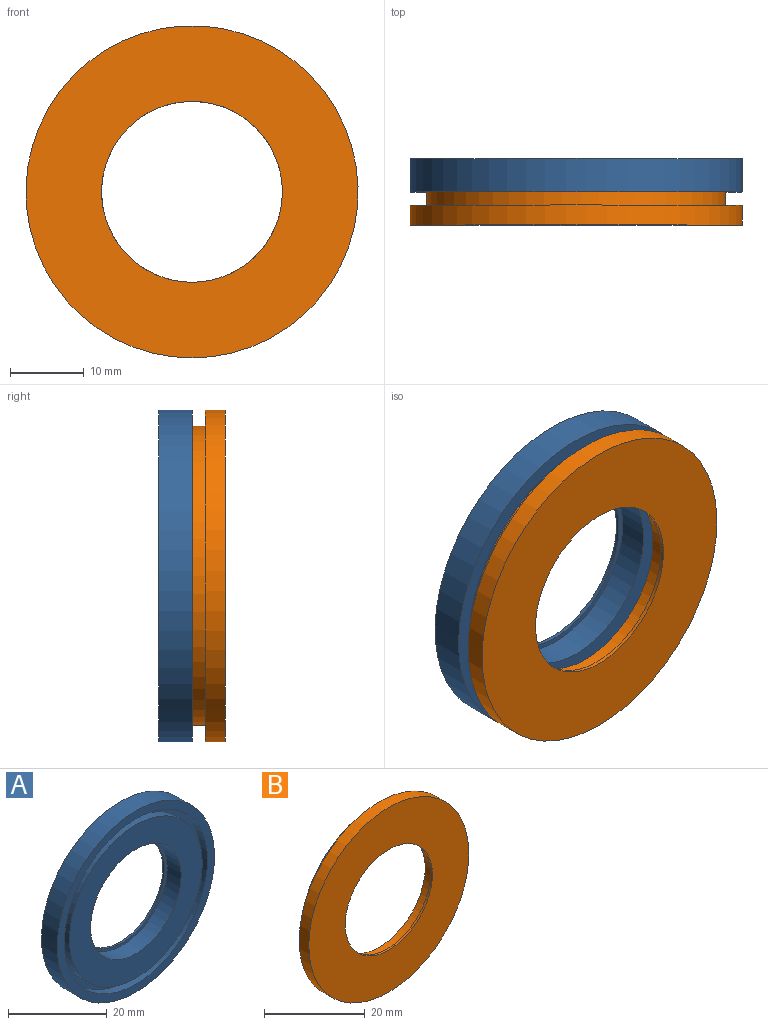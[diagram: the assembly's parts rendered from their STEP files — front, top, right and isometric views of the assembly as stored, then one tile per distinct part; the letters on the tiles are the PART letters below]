
ASSEMBLY  parts=2 mates=1
PART A: 10 faces, bbox 45x4.5x45 mm
  f0: plane 38x38mm, normal (0,-1,0), area 607.3mm2, adj f1,f7
  f1: cylinder r=12.95mm len=25.9mm, axis (0,1,0), area 325.5mm2, adj f0,f6
  f2: cylinder r=22.5mm len=45mm, axis (0,1,0), area 636.2mm2, adj f3,f4
  f3: plane 45x45mm, normal (0,-1,0), area 270.2mm2, adj f2,f8
  f4: plane 45x45mm, normal (0,1,0), area 1119mm2, adj f2,f5
  f5: cylinder r=12.25mm len=24.5mm, axis (0,1,0), area 38.5mm2, adj f4,f6
  f6: plane 25.9x25.9mm, normal (0,-1,0), area 55.4mm2, adj f1,f5
  f7: cylinder r=19mm len=38mm, axis (0,-1,0), area 238.8mm2, adj f0,f9
  f8: cylinder r=20.5mm len=41mm, axis (0,-1,0), area 257.6mm2, adj f3,f9
  f9: plane 41x41mm, normal (0,-1,0), area 186.1mm2, adj f7,f8
PART B: 10 faces, bbox 45x4.5x45 mm
  f0: plane 38.5x38.5mm, normal (0,1,0), area 637.3mm2, adj f1,f7
  f1: cylinder r=12.95mm len=25.9mm, axis (0,1,0), area 179mm2, adj f0,f6
  f2: cylinder r=22.5mm len=45mm, axis (0,1,0), area 381.7mm2, adj f3,f4
  f3: plane 45x45mm, normal (0,-1,0), area 1119mm2, adj f2,f5
  f4: plane 45x45mm, normal (0,1,0), area 302.2mm2, adj f2,f8
  f5: cylinder r=12.25mm len=24.5mm, axis (0,-1,0), area 38.5mm2, adj f3,f6
  f6: plane 25.9x25.9mm, normal (0,1,0), area 55.4mm2, adj f1,f5
  f7: cylinder r=19.25mm len=38.5mm, axis (0,-1,0), area 217.7mm2, adj f0,f9
  f8: cylinder r=20.25mm len=40.5mm, axis (0,-1,0), area 229mm2, adj f4,f9
  f9: plane 40.5x40.5mm, normal (0,1,0), area 124.1mm2, adj f7,f8
PLACE A t=(-10,-2.72,-5.54)mm
PLACE B t=(-10,-9.02,-5.54)mm
MATE fastened A.f5 <-> B.f5  axis (0,-1,0) through (-10,-7.22,-5.54)mm
